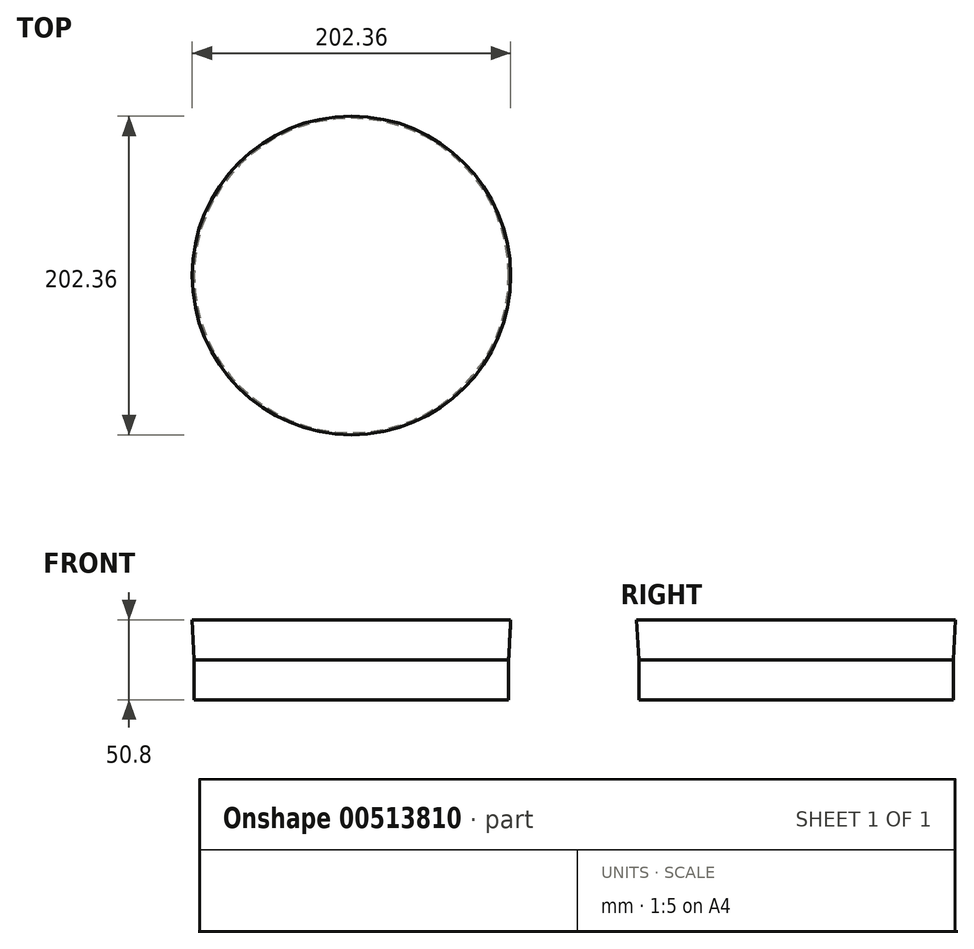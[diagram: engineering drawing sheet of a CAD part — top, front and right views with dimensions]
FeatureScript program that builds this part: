
annotation { "Feature Type Name" : "Feature", "Feature Type Description" : "" }
export const myFeature = defineFeature(function(context is Context, id is Id, definition is map)
    precondition{}
    {
        {
            var Q0;
            Q0=qCreatedBy(makeId("Top.planeOp"),FACE);
            var sketch = newSketch(context, id + "F0", { "sketchPlane" : qUnion([Q0])});
            skCircle(sketch, "E0", {"center": v(0, 0) * mm, "radius": 99.85 * mm});
            skSolve(sketch);
        }
        {
            var Q0;
            Q0=makeQuery(id+"F0.imprint","IMPRINT",FACE,{"disambiguationData":[TD([[makeQuery(id+"F0.imprint","IMPRINT",EDGE,{"derivedFrom":sQuery(id+"F0.wireOp",EDGE,"E0")}),1.0]])]});
            extrude(context, id + "F1", {"entities" : qUnion([Q0]), "depth" : 25.4 * mm, "hasDraft" : true, "draftAngle" : 3 * degree, "hasSecondDirection" : true, "secondDirectionOppositeDirection" : true, "secondDirectionDepth" : 25.4 * mm});
        }
    });
